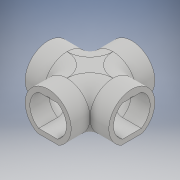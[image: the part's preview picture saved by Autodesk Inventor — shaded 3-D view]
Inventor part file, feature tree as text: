
AUTODESK INVENTOR PART (.ipt)
format: ipt  version: 2017 (Build 210142000, 142)  size: 487,424 bytes
history: native  units: in
note: dims shown in document units (in); Inventor stores cm internally (conversion verified against a paired STEP export)
features: sketch x6, extrude x5, mirror x4, other x3, sweep x2, plane x1, fillet x1
ambient origin geometry x8: Origin, YZ Plane, XZ Plane, XY Plane, X Axis, Y Axis, Z Axis, Center Point
bodies: Body1 (feature_tree), Body2 (feature_tree), Body3 (feature_tree)
feature tree (22):
  sketch  "Sketch1"  dims[d0=6.6667in d2=9.7746in d5=-4.8873in d49=0.0625in]
  extrude  "corridor eighth"  Depth=0.0625in
  plane  "Work Plane1"
  extrude  "light quarter eighth"  Depth=4.0in TaperAngle=0.0deg
  sketch  "Sketch17"  dims[d153=0.25in d154=0.0417in]
  sketch  "Sketch7"  dims[d62=45.0deg d71=4.0in d72=0.0in]
  sweep  "sweep corridor quarter"
  sweep  "light sweep quarter"
  mirror  "mirror plane YZ"
  mirror  "mirror plane XY"
  mirror  "mirror corridor half"
  mirror  "mirror corridor full"
  extrude  "top hole fill"  Depth=4.0in TaperAngle=0.0deg
  extrude  "top fill in for light"  TaperAngle=0.0deg  [1 undecoded]
  fillet  "Fillet1"  [1 undecoded]
  extrude  "bottom hole fill in"  Depth=0.0625in TaperAngle=0.0deg
  other  "corridor"
  other  "light eighth"
  other  "light forth"
  sketch  "Sketch19"  dims[d155=0.0625in d156=0.0892in]
  sketch  "Sketch20"  dims[d157=0.125in d158=4.0in d159=0.0in]
  sketch  "Sketch21"  dims[d160=4.0in d161=0.0in d162=0.0in d163=0.0in d164=0.0in d165=1.429in d166=0.0in d167=1.554in d168=10.3167in d169=10.3167in d170=10.3167in d171=10.3167in d172=5.1583in d173=5.1583in d174=5.1583in d175=5.1583in d176=0.125in d177=0.0in d178=0.0625in d179=1.0in d180=0.0in]
note: 2 required parameter values undecoded (feature->parameter linkage not recoverable at this tier; creation-order binding heuristic only, values carry confidence <= 0.55)
